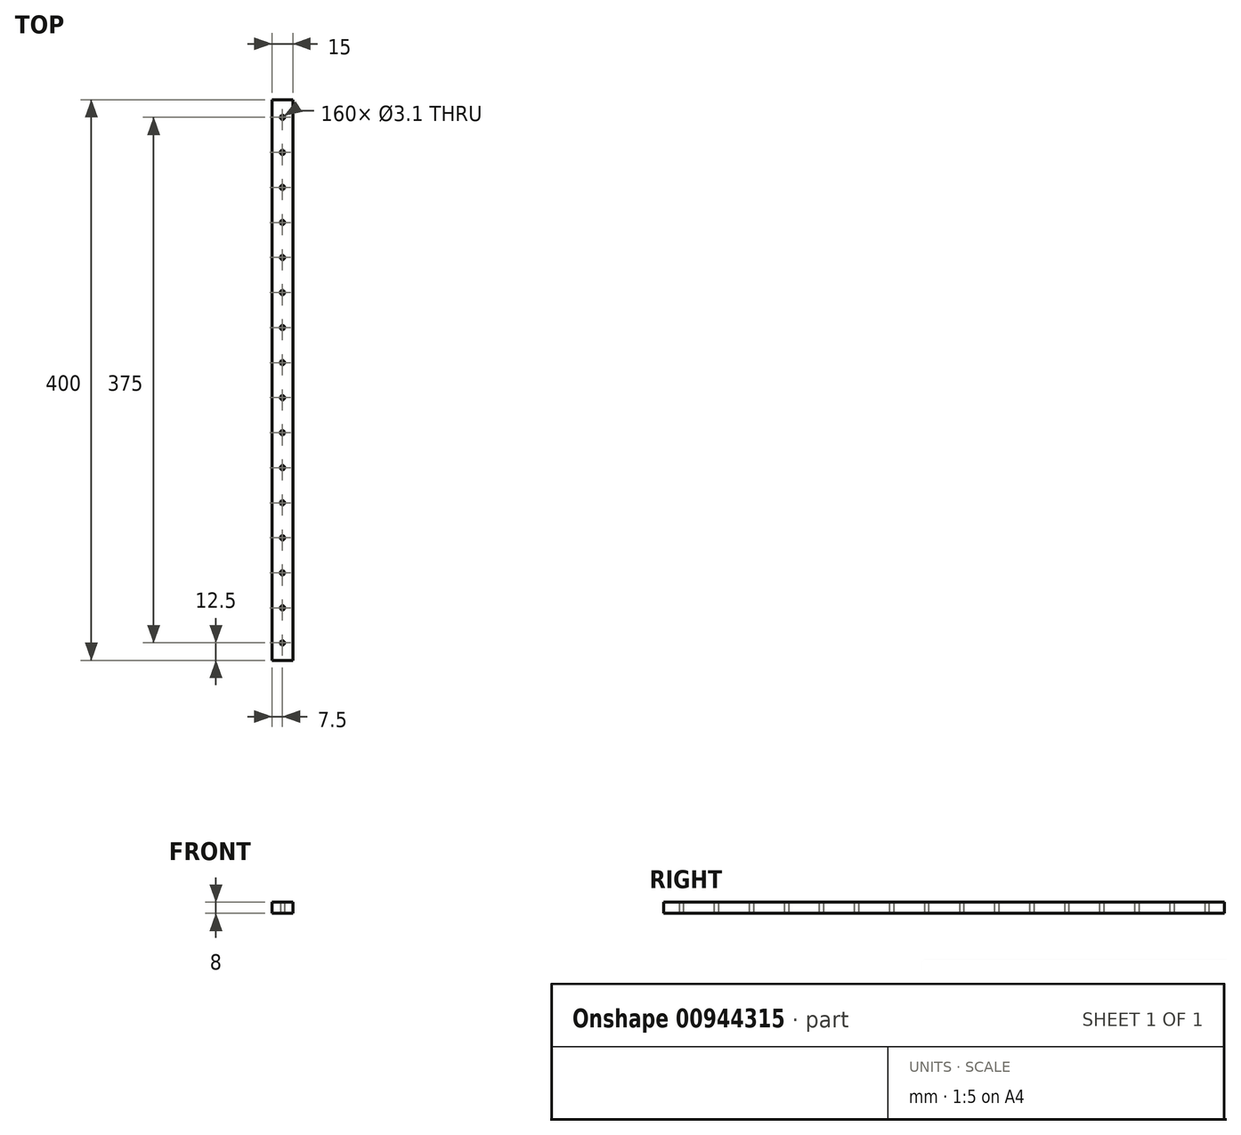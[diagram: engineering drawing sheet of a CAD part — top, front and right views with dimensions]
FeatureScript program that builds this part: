
annotation { "Feature Type Name" : "Feature", "Feature Type Description" : "" }
export const myFeature = defineFeature(function(context is Context, id is Id, definition is map)
    precondition{}
    {
        {
            var Q0;
            Q0=qCreatedBy(makeId("Top.planeOp"),FACE);
            var sketch = newSketch(context, id + "F0", { "sketchPlane" : qUnion([Q0])});
            skLineSegment(sketch, "E0.bottom", {"start": v(7.5, -200) * mm, "end": v(-7.5, -200) * mm});
            skLineSegment(sketch, "E0.top", {"start": v(7.5, 200) * mm, "end": v(-7.5, 200) * mm});
            skLineSegment(sketch, "E0.left", {"start": v(7.5, -200) * mm, "end": v(7.5, 200) * mm});
            skLineSegment(sketch, "E0.right", {"start": v(-7.5, -200) * mm, "end": v(-7.5, 200) * mm});
            skPoint(sketch, "E0.middle", {"position": v(0, 0) * mm});
            skLineSegment(sketch, "E1", {"start": v(0, -200) * mm, "end": v(0, 200) * mm, "construction": true});
            skLineSegment(sketch, "E2", {"start": v(-80.46, 187.5) * mm, "end": v(92.95, 187.5) * mm, "construction": true});
            skCircle(sketch, "E3", {"center": v(0, 187.5) * mm, "radius": 1.55 * mm});
            skCircle(sketch, "E4.1.0.0", {"center": v(0, 162.5) * mm, "radius": 1.55 * mm});
            skCircle(sketch, "E4.2.0.0", {"center": v(0, 137.5) * mm, "radius": 1.55 * mm});
            skCircle(sketch, "E4.3.0.0", {"center": v(0, 112.5) * mm, "radius": 1.55 * mm});
            skCircle(sketch, "E4.4.0.0", {"center": v(0, 87.5) * mm, "radius": 1.55 * mm});
            skCircle(sketch, "E4.5.0.0", {"center": v(0, 62.5) * mm, "radius": 1.55 * mm});
            skCircle(sketch, "E4.6.0.0", {"center": v(0, 37.5) * mm, "radius": 1.55 * mm});
            skCircle(sketch, "E4.7.0.0", {"center": v(0, 12.5) * mm, "radius": 1.55 * mm});
            skCircle(sketch, "E4.8.0.0", {"center": v(0, -12.5) * mm, "radius": 1.55 * mm});
            skCircle(sketch, "E4.9.0.0", {"center": v(0, -37.5) * mm, "radius": 1.55 * mm});
            skCircle(sketch, "E4.10.0.0", {"center": v(0, -62.5) * mm, "radius": 1.55 * mm});
            skCircle(sketch, "E4.11.0.0", {"center": v(0, -87.5) * mm, "radius": 1.55 * mm});
            skCircle(sketch, "E4.12.0.0", {"center": v(0, -112.5) * mm, "radius": 1.55 * mm});
            skCircle(sketch, "E4.13.0.0", {"center": v(0, -137.5) * mm, "radius": 1.55 * mm});
            skCircle(sketch, "E4.14.0.0", {"center": v(0, -162.5) * mm, "radius": 1.55 * mm});
            skCircle(sketch, "E4.15.0.0", {"center": v(0, -187.5) * mm, "radius": 1.55 * mm});
            skLineSegment(sketch, "E4.direction1", {"start": v(0, 187.5) * mm, "end": v(0, 162.5) * mm, "construction": true});
            skSolve(sketch);
        }
        {
            var Q0;
            Q0=makeQuery(id+"F0.imprint","IMPRINT",FACE,{"disambiguationData":[TD([[makeQuery(id+"F0.imprint","IMPRINT",EDGE,{"derivedFrom":sQuery(id+"F0.wireOp",EDGE,"E0.bottom")}),-1.0]])]});
            extrude(context, id + "F1", {"entities" : qUnion([Q0]), "depth" : 8 * mm, "offsetDistance" : 25 * mm});
        }
    });
